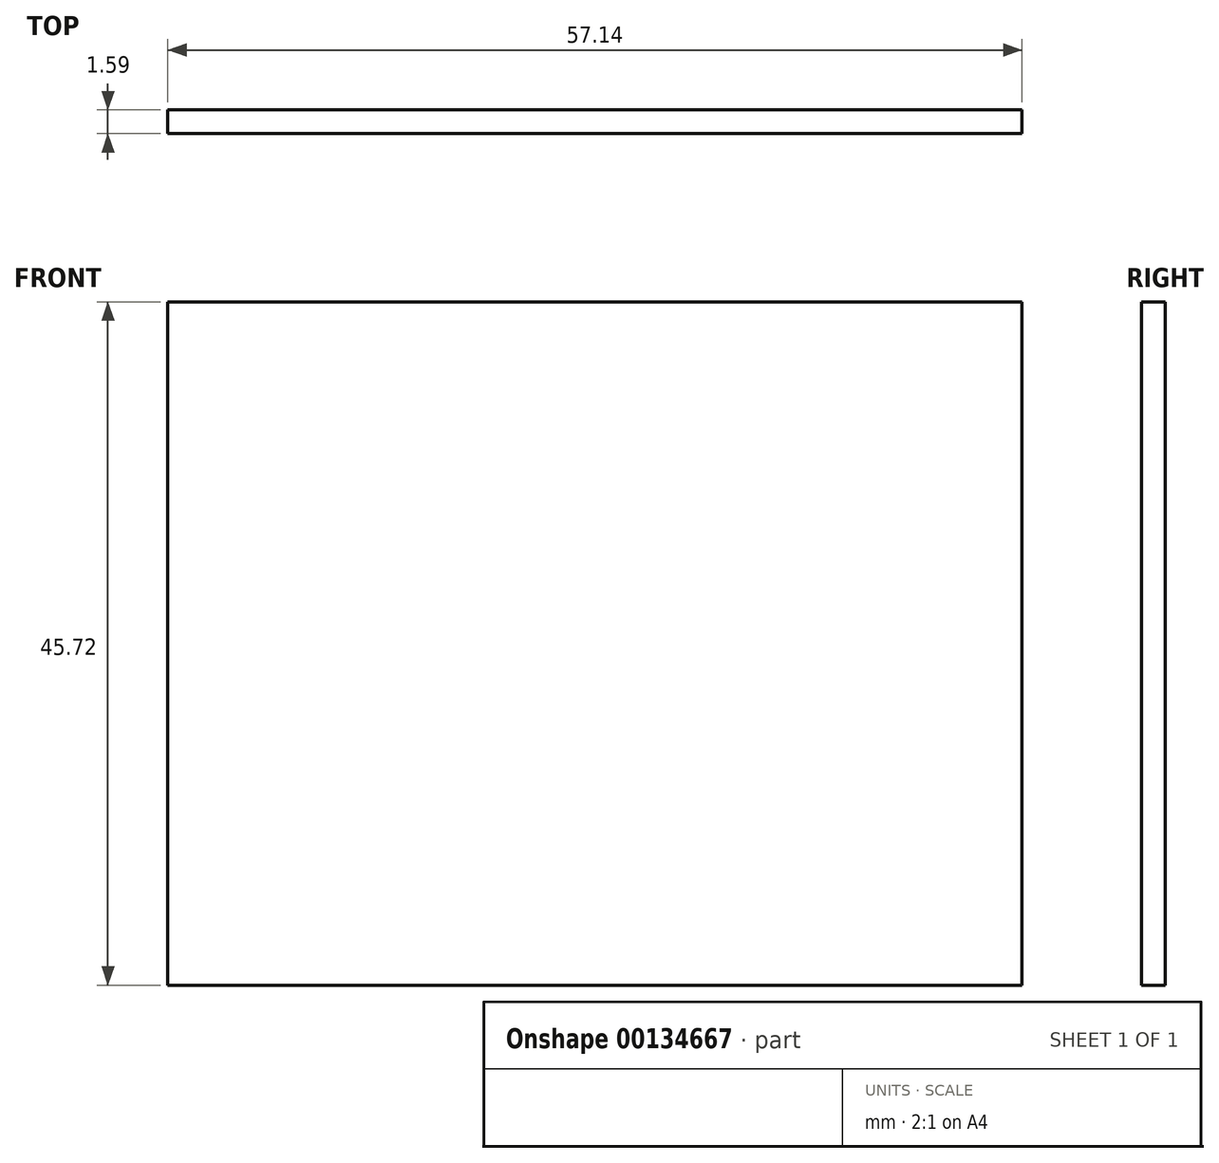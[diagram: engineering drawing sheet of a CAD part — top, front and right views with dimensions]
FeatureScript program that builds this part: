
annotation { "Feature Type Name" : "Feature", "Feature Type Description" : "" }
export const myFeature = defineFeature(function(context is Context, id is Id, definition is map)
    precondition{}
    {
        {
            var Q0;
            Q0=qCreatedBy(makeId("Front.planeOp"),FACE);
            var sketch = newSketch(context, id + "F0", { "sketchPlane" : qUnion([Q0])});
            skLineSegment(sketch, "E0.bottom", {"start": v(-28.58, -22.86) * mm, "end": v(28.58, -22.86) * mm});
            skLineSegment(sketch, "E0.top", {"start": v(-28.58, 22.86) * mm, "end": v(28.57, 22.86) * mm});
            skLineSegment(sketch, "E0.left", {"start": v(-28.57, -22.86) * mm, "end": v(-28.58, 22.86) * mm});
            skLineSegment(sketch, "E0.right", {"start": v(28.58, -22.86) * mm, "end": v(28.57, 22.86) * mm});
            skPoint(sketch, "E0.middle", {"position": v(0, 0) * mm});
            skSolve(sketch);
        }
        {
            var Q0;
            Q0 = qSketchRegion(id + "F0", true);
            extrude(context, id + "F1", {"entities" : qUnion([Q0]), "depth" : 1.59 * mm});
        }
    });
